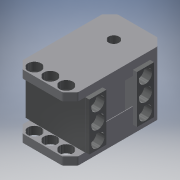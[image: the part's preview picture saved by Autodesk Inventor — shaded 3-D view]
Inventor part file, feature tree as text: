
AUTODESK INVENTOR PART (.ipt)
format: ipt  version: 2017 (Build 210142000, 142)  size: 338,944 bytes
history: native  units: mm
features: extrude x13, sketch x13, fillet x1, chamfer x1
ambient origin geometry x8: Origin, YZ Plane, XZ Plane, XY Plane, X Axis, Y Axis, Z Axis, Center Point
bodies: Solide1 (feature_tree)
feature tree (28):
  extrude  "Extrusion1"  Depth=15.0mm
  extrude  "Extrusion2"  Depth=21.0mm
  extrude  "Extrusion3"  Depth=36.0mm
  extrude  "Extrusion4"  Depth=24.0mm TaperAngle=0.0deg
  extrude  "Extrusion6"  Depth=3.0mm
  extrude  "Extrusion7"  Depth=5.6mm
  extrude  "Extrusion8"  Depth=24.0mm TaperAngle=0.0deg
  extrude  "Extrusion9"  Depth=0.5mm
  extrude  "Extrusion10"  Depth=5.0mm
  extrude  "Extrusion11"  Depth=6.0mm
  extrude  "Extrusion12"  Depth=24.0mm TaperAngle=0.0deg
  extrude  "Extrusion13"  Depth=5.0mm
  extrude  "Extrusion14"  Depth=24.0mm
  fillet  "Congé1"  Radius=6.0mm
  chamfer  "Chanfrein1"  Distance=3.0mm
  sketch  "Esquisse2"
  sketch  "Esquisse3"
  sketch  "Esquisse4"
  sketch  "Esquisse5"
  sketch  "Esquisse7"
  sketch  "Esquisse8"
  sketch  "Esquisse9"
  sketch  "Esquisse10"
  sketch  "Esquisse11"
  sketch  "Esquisse13"
  sketch  "Esquisse14"
  sketch  "Esquisse16"
  sketch  "Esquisse17"
